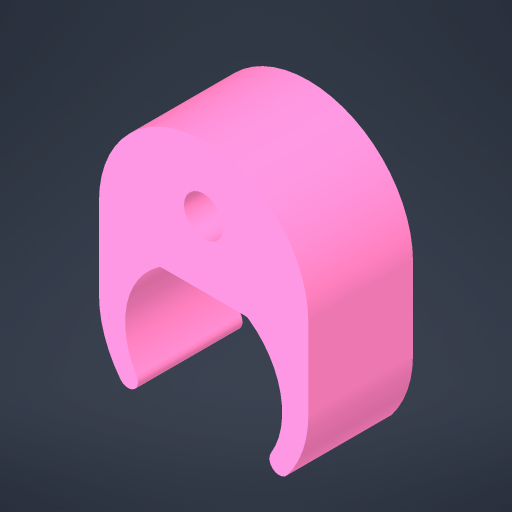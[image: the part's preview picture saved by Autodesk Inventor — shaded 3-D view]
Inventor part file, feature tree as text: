
AUTODESK INVENTOR PART (.ipt)
format: ipt  version: 2023.4 (Build 274418000, 418)  size: 278,016 bytes
history: native  units: mm
features: reference x6, other x4, sketch x2, extrude x2, plane x1, fillet x1, projected_geometry x1
ambient origin geometry x8: Origin, YZ Plane, XZ Plane, XY Plane, X Axis, Y Axis, Z Axis, Center Point
bodies: Solid1 (feature_tree)
feature tree (17):
  sketch  "Sketch1"  dims[d0=2.0mm d2=3.0mm d3=6.0mm]
  plane  "Work Plane1"
  extrude  "Extrusion1"  Depth=3.0mm
  fillet  "Fillet1"  Radius=6.0mm
  extrude  "Extrusion2"  Depth=0.75mm
  reference  "Reference1"
  reference  "Reference8"
  reference  "Reference9"
  reference  "Reference10"
  reference  "Reference11"
  reference  "Reference12"
  sketch  "Sketch2"  dims[d4=6.0mm d5=0.0mm d6=0.75mm d7=6.0mm d8=2.0mm d9=0.0mm d10=10.0mm]
  projected_geometry  "Projected Loop1"
  parser-record x1  (decoder bookkeeping rows leaked as tree rows — omitted from the tree; the rows remain in map.json)
  other  "XYZ Stage V5.iam"
  other  "Z Stage Part V5:1"
  other  "DC Motor:2"
note: 1 file-system path scrubbed to <path> (originals preserved in map.json)
